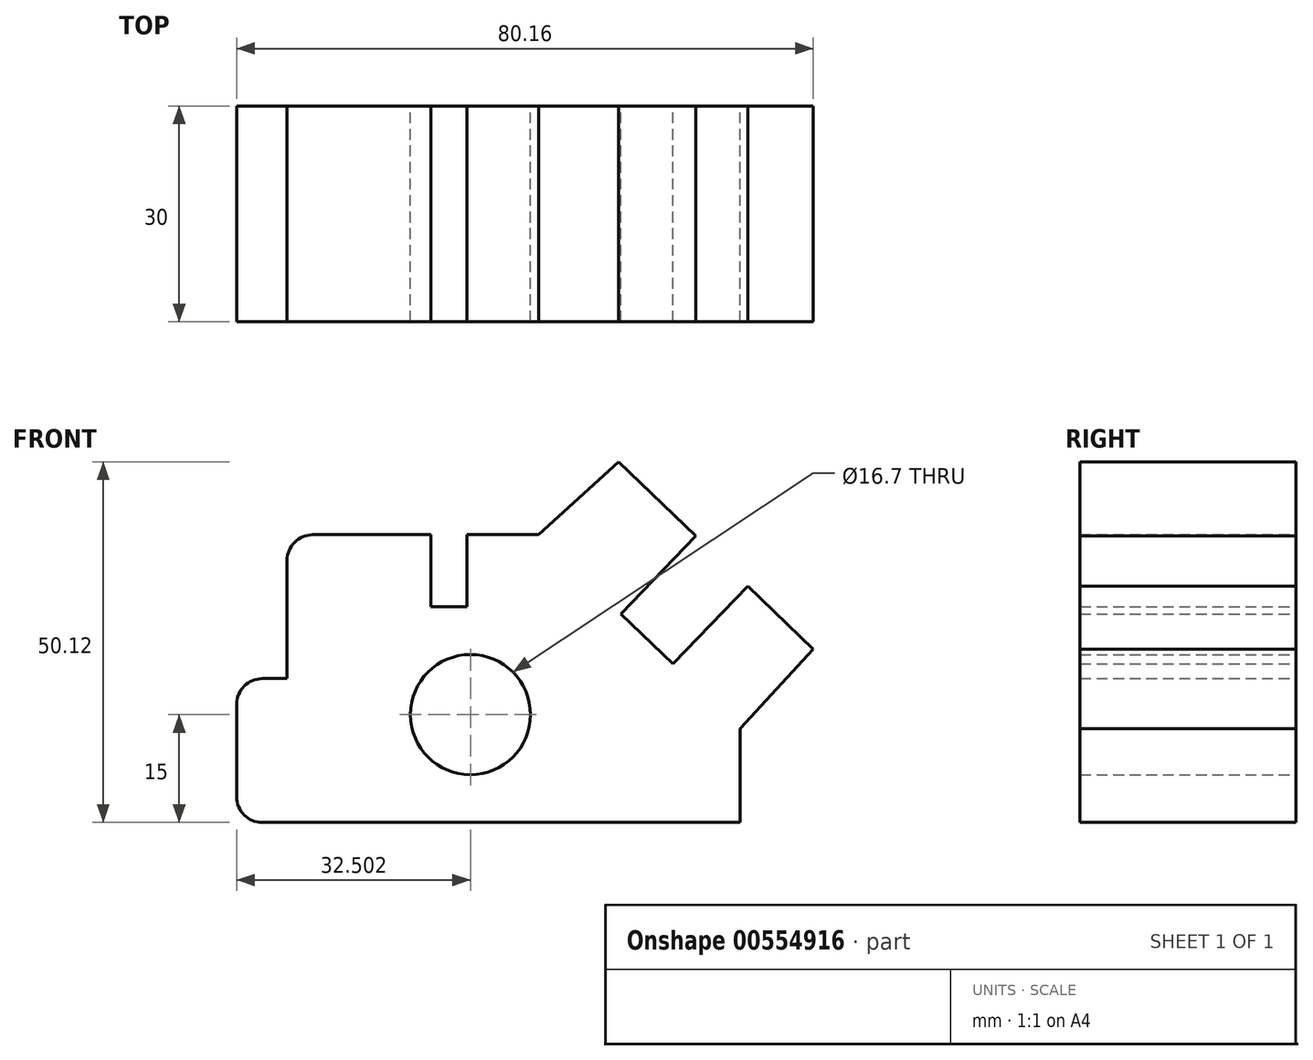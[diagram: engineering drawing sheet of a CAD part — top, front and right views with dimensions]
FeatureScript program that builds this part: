
annotation { "Feature Type Name" : "Feature", "Feature Type Description" : "" }
export const myFeature = defineFeature(function(context is Context, id is Id, definition is map)
    precondition{}
    {
        {
            var Q0;
            Q0=qCreatedBy(makeId("Front.planeOp"),FACE);
            var sketch = newSketch(context, id + "F0", { "sketchPlane" : qUnion([Q0])});
            skLineSegment(sketch, "E0", {"start": v(11.77, -25.54) * mm, "end": v(-54.66, -25.54) * mm});
            skLineSegment(sketch, "E1", {"start": v(-58.23, -21.97) * mm, "end": v(-58.23, -9.11) * mm});
            skLineSegment(sketch, "E2", {"start": v(-54.66, -5.54) * mm, "end": v(-51.23, -5.54) * mm});
            skLineSegment(sketch, "E3", {"start": v(-51.23, -5.54) * mm, "end": v(-51.23, 10.89) * mm});
            skLineSegment(sketch, "E4", {"start": v(-47.66, 14.46) * mm, "end": v(-31.23, 14.46) * mm});
            skLineSegment(sketch, "E5", {"start": v(-31.23, 14.46) * mm, "end": v(-31.23, 4.46) * mm});
            skLineSegment(sketch, "E6", {"start": v(-31.23, 4.46) * mm, "end": v(-26.23, 4.46) * mm});
            skLineSegment(sketch, "E7", {"start": v(-26.23, 4.46) * mm, "end": v(-26.23, 14.46) * mm});
            skLineSegment(sketch, "E8", {"start": v(-26.23, 14.46) * mm, "end": v(-16.23, 14.46) * mm});
            skLineSegment(sketch, "E9", {"start": v(11.77, -25.54) * mm, "end": v(11.77, -12.47) * mm});
            skLineSegment(sketch, "E10", {"start": v(-4.8, 3.47) * mm, "end": v(2.4, -3.47) * mm});
            skPoint(sketch, "E11", {"position": v(-1.2, 0) * mm});
            skPoint(sketch, "E12", {"position": v(-4.8, 3.47) * mm});
            skCircle(sketch, "E13", {"center": v(-25.73, -10.54) * mm, "radius": 8.35 * mm});
            skPoint(sketch, "E14", {"position": v(2.4, -3.47) * mm});
            skLineSegment(sketch, "E15", {"start": v(-4.8, 3.47) * mm, "end": v(5.6, 14.28) * mm});
            skLineSegment(sketch, "E16", {"start": v(5.6, 14.28) * mm, "end": v(-5.11, 24.58) * mm});
            skLineSegment(sketch, "E17", {"start": v(-5.11, 24.58) * mm, "end": v(-16.23, 14.46) * mm});
            skLineSegment(sketch, "E18", {"start": v(2.4, -3.47) * mm, "end": v(12.8, 7.34) * mm});
            skLineSegment(sketch, "E19", {"start": v(12.8, 7.34) * mm, "end": v(21.93, -1.44) * mm});
            skLineSegment(sketch, "E20", {"start": v(21.93, -1.44) * mm, "end": v(11.77, -12.47) * mm});
            skPoint(sketch, "E21.visualSharp", {"position": v(-51.23, 14.46) * mm});
            skArc(sketch, "E21.filletArc", {"start": v(-47.66, 14.46) * mm, "mid": v(-50.18, 13.41) * mm, "end": v(-51.23, 10.89) * mm});
            skPoint(sketch, "E22.visualSharp", {"position": v(-58.23, -5.54) * mm});
            skArc(sketch, "E22.filletArc", {"start": v(-54.66, -5.54) * mm, "mid": v(-57.18, -6.59) * mm, "end": v(-58.23, -9.11) * mm});
            skPoint(sketch, "E23.visualSharp", {"position": v(-58.23, -25.54) * mm});
            skArc(sketch, "E23.filletArc", {"start": v(-58.23, -21.97) * mm, "mid": v(-57.18, -24.5) * mm, "end": v(-54.66, -25.54) * mm});
            skSolve(sketch);
        }
        {
            var Q0;
            Q0 = qSketchRegion(id + "F0", true);
            extrude(context, id + "F1", {"entities" : qUnion([Q0]), "depth" : 30 * mm, "offsetDistance" : 25 * mm});
        }
    });
